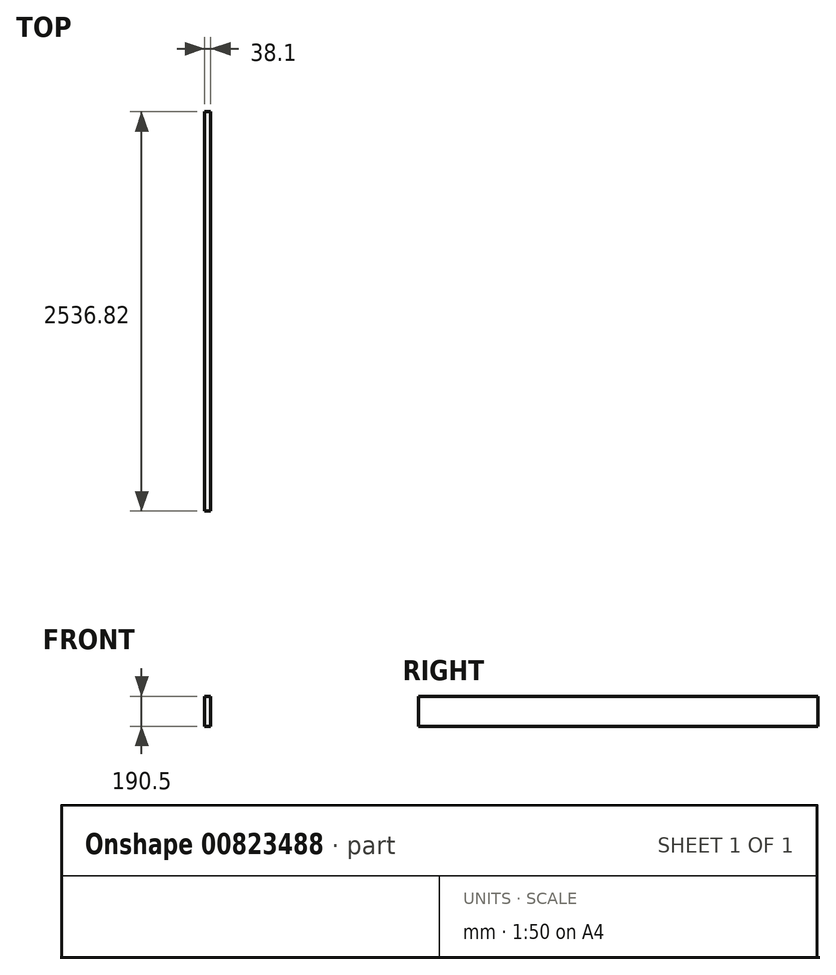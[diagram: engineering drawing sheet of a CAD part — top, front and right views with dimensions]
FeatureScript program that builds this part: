
annotation { "Feature Type Name" : "Feature", "Feature Type Description" : "" }
export const myFeature = defineFeature(function(context is Context, id is Id, definition is map)
    precondition{}
    {
        {
            var Q0;
            Q0=qCreatedBy(makeId("Front.planeOp"),FACE);
            var sketch = newSketch(context, id + "F0", { "sketchPlane" : qUnion([Q0])});
            skLineSegment(sketch, "E0.bottom", {"start": v(0, 0) * mm, "end": v(38.1, 0) * mm});
            skLineSegment(sketch, "E0.top", {"start": v(0, 190.5) * mm, "end": v(38.1, 190.5) * mm});
            skLineSegment(sketch, "E0.left", {"start": v(0, 0) * mm, "end": v(0, 190.5) * mm});
            skLineSegment(sketch, "E0.right", {"start": v(38.1, 0) * mm, "end": v(38.1, 190.5) * mm});
            skSolve(sketch);
        }
        {
            var Q0;
            Q0=qSketchRegion(id+"F0",true);
            extrude(context, id + "F1", {"entities" : qUnion([Q0]), "depth" : 2536.82 * mm, "offsetDistance" : 25.4 * mm});
        }
    });
